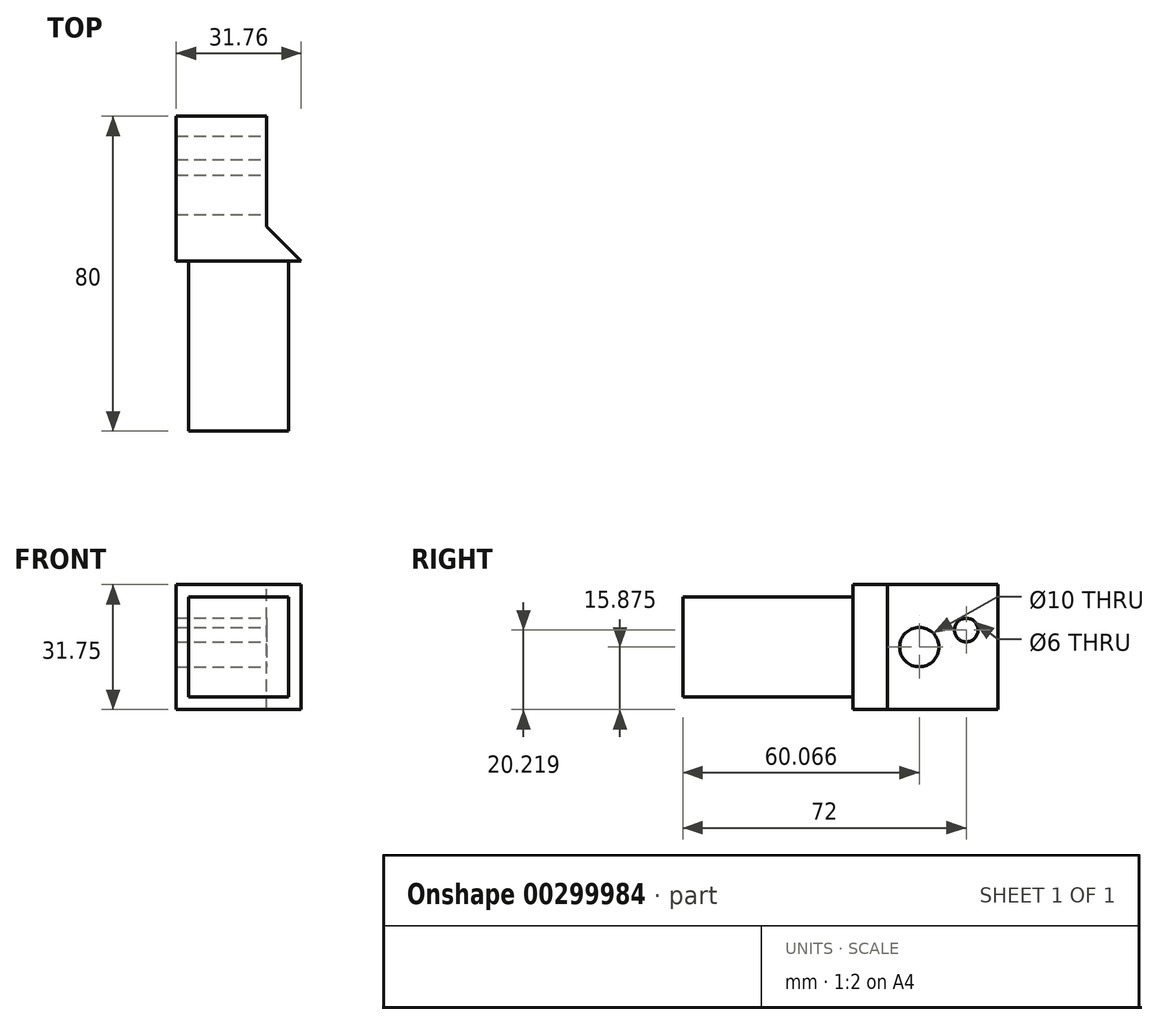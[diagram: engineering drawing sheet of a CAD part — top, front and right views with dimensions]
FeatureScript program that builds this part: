
annotation { "Feature Type Name" : "Feature", "Feature Type Description" : "" }
export const myFeature = defineFeature(function(context is Context, id is Id, definition is map)
    precondition{}
    {
        {
            var Q0;
            Q0=qCreatedBy(makeId("Top.planeOp"),FACE);
            var sketch = newSketch(context, id + "F0", { "sketchPlane" : qUnion([Q0])});
            skLineSegment(sketch, "E0.bottom", {"start": v(-15.88, 40) * mm, "end": v(15.88, 40) * mm});
            skLineSegment(sketch, "E0.top", {"start": v(-15.88, -40) * mm, "end": v(15.88, -40) * mm});
            skLineSegment(sketch, "E0.left", {"start": v(-15.88, 40) * mm, "end": v(-15.88, -40) * mm});
            skLineSegment(sketch, "E0.right", {"start": v(15.88, 40) * mm, "end": v(15.88, -40) * mm});
            skSolve(sketch);
        }
        {
            var Q0;
            Q0 = qSketchRegion(id + "F0", true);
            extrude(context, id + "F1", {"entities" : qUnion([Q0]), "depth" : 31.75 * mm, "offsetDistance" : 25 * mm});
        }
        {
            var Q0;
            Q0=makeQuery(id+"F1.opExtrude","SWEPT_FACE",FACE,{"disambiguationData":[OSD([sQuery(id+"F0.wireOp",EDGE,"E0.right")])]});
            var sketch = newSketch(context, id + "F2", { "sketchPlane" : qUnion([Q0])});
            skCircle(sketch, "E1", {"center": v(20.07, 15.88) * mm, "radius": 5 * mm});
            skCircle(sketch, "E2", {"center": v(32, 20.22) * mm, "radius": 3 * mm});
            skLineSegment(sketch, "E3", {"start": v(20.07, 15.88) * mm, "end": v(26.86, 15.88) * mm});
            skLineSegment(sketch, "E4", {"start": v(20.07, 15.88) * mm, "end": v(32, 20.22) * mm});
            skSolve(sketch);
        }
        {
            var Q0;
            Q0 = qSketchRegion(id + "F2", true);
            extrude(context, id + "F3", {"entities" : qUnion([Q0]), "operationType" : NewBodyOperationType.REMOVE, "endBound" : BoundingType.THROUGH_ALL, "oppositeDirection" : true, "depth" : 25 * mm, "offsetDistance" : 25 * mm});
        }
        {
            var Q0;
            Q0=makeQuery(id+"F1.opExtrude","CAP_FACE",FACE,{"disambiguationData":[OSD([sQuery(id+"F0.wireOp",EDGE,"E0.bottom"),sQuery(id+"F0.wireOp",EDGE,"E0.top"),sQuery(id+"F0.wireOp",EDGE,"E0.left"),sQuery(id+"F0.wireOp",EDGE,"E0.right")])],"isStart":false});
            var sketch = newSketch(context, id + "F4", { "sketchPlane" : qUnion([Q0])});
            skLineSegment(sketch, "E5", {"start": v(-12.7, -50) * mm, "end": v(-12.7, 10) * mm});
            skLineSegment(sketch, "E6", {"start": v(-12.7, 10) * mm, "end": v(12.7, 10) * mm});
            skLineSegment(sketch, "E7", {"start": v(12.7, 10) * mm, "end": v(12.7, -50) * mm});
            skLineSegment(sketch, "E8", {"start": v(12.7, -50) * mm, "end": v(-12.7, -50) * mm});
            skLineSegment(sketch, "E9", {"start": v(15.88, 40) * mm, "end": v(15.88, -63.27) * mm});
            skLineSegment(sketch, "E10", {"start": v(-12.7, 3.25) * mm, "end": v(-28.39, 3.25) * mm});
            skLineSegment(sketch, "E11", {"start": v(-28.39, 3.25) * mm, "end": v(29.3, 3.25) * mm});
            skLineSegment(sketch, "E12", {"start": v(29.3, 3.25) * mm, "end": v(29.3, -68.48) * mm});
            skLineSegment(sketch, "E13", {"start": v(29.3, -68.48) * mm, "end": v(-28.39, -68.48) * mm});
            skLineSegment(sketch, "E14", {"start": v(-28.39, -68.48) * mm, "end": v(-28.39, 3.25) * mm});
            skSolve(sketch);
        }
        {
            var Q0;
            {var subQ0=sQuery(id+"F4.wireOp",EDGE,"E8");Q0=makeQuery(id+"F4.imprint","IMPRINT",FACE,{"disambiguationData":[TD([[makeQuery(id+"F4.imprint","IMPRINT",EDGE,{"derivedFrom":subQ0}),-1.0]])]});}
            var Q1;
            {var subQ0=sQuery(id+"F4.wireOp",EDGE,"E11");var subQ1=sQuery(id+"F4.wireOp",EDGE,"E7");var subQ2=makeQuery(id+"F4.imprint","INTERSECT",VERTEX,{"derivedFrom":[subQ1,subQ0]});Q1=makeQuery(id+"F4.imprint","IMPRINT",FACE,{"disambiguationData":[TD([[makeQuery(id+"F4.imprint","IMPRINT",EDGE,{"disambiguationData":[TD([[subQ2,-1.0]])],"derivedFrom":subQ1}),1.0]])]});}
            var Q2;
            {var subQ0=sQuery(id+"F4.wireOp",EDGE,"E11");var subQ1=sQuery(id+"F4.wireOp",EDGE,"E5");var subQ2=makeQuery(id+"F4.imprint","INTERSECT",VERTEX,{"derivedFrom":[subQ1,subQ0]});Q2=makeQuery(id+"F4.imprint","IMPRINT",FACE,{"disambiguationData":[TD([[makeQuery(id+"F4.imprint","IMPRINT",EDGE,{"disambiguationData":[TD([[subQ2,1.0]])],"derivedFrom":subQ1}),1.0]])]});}
            extrude(context, id + "F5", {"entities" : qUnion([Q0, Q1, Q2]), "operationType" : NewBodyOperationType.REMOVE, "endBound" : BoundingType.THROUGH_ALL, "oppositeDirection" : true, "depth" : 25 * mm, "offsetDistance" : 25 * mm});
        }
        {
            var Q0;
            Q0=makeQuery(id+"F1.opExtrude","SWEPT_FACE",FACE,{"disambiguationData":[OSD([sQuery(id+"F0.wireOp",EDGE,"E0.right")])]});
            var sketch = newSketch(context, id + "F6", { "sketchPlane" : qUnion([Q0])});
            skLineSegment(sketch, "E15.bottom", {"start": v(3.25, 28.58) * mm, "end": v(-44.46, 28.57) * mm});
            skLineSegment(sketch, "E15.top", {"start": v(3.25, 40.72) * mm, "end": v(-44.46, 40.72) * mm});
            skLineSegment(sketch, "E15.left", {"start": v(3.25, 28.57) * mm, "end": v(3.25, 40.72) * mm});
            skLineSegment(sketch, "E15.right", {"start": v(-44.46, 28.57) * mm, "end": v(-44.46, 40.72) * mm});
            skLineSegment(sketch, "E16.bottom", {"start": v(3.25, 3.17) * mm, "end": v(-44.46, 3.17) * mm});
            skLineSegment(sketch, "E16.top", {"start": v(3.25, -7.24) * mm, "end": v(-44.46, -7.24) * mm});
            skLineSegment(sketch, "E16.left", {"start": v(3.25, 3.17) * mm, "end": v(3.25, -7.24) * mm});
            skLineSegment(sketch, "E16.right", {"start": v(-44.46, 3.17) * mm, "end": v(-44.46, -7.24) * mm});
            skSolve(sketch);
        }
        {
            var Q0;
            Q0 = qSketchRegion(id + "F6", true);
            extrude(context, id + "F7", {"entities" : qUnion([Q0]), "operationType" : NewBodyOperationType.REMOVE, "endBound" : BoundingType.THROUGH_ALL, "oppositeDirection" : true, "depth" : 25 * mm, "offsetDistance" : 25 * mm});
        }
        {
            var Q0;
            Q0=makeQuery(id+"F1.opExtrude","CAP_FACE",FACE,{"disambiguationData":[OSD([sQuery(id+"F0.wireOp",EDGE,"E0.bottom"),sQuery(id+"F0.wireOp",EDGE,"E0.top"),sQuery(id+"F0.wireOp",EDGE,"E0.left"),sQuery(id+"F0.wireOp",EDGE,"E0.right")])],"isStart":false});
            var sketch = newSketch(context, id + "F8", { "sketchPlane" : qUnion([Q0])});
            skLineSegment(sketch, "E17.bottom", {"start": v(15.88, 40) * mm, "end": v(7.12, 40) * mm});
            skLineSegment(sketch, "E17.top", {"start": v(15.88, 3.25) * mm, "end": v(7.12, 3.25) * mm});
            skLineSegment(sketch, "E17.left", {"start": v(15.88, 40) * mm, "end": v(15.88, 3.25) * mm});
            skLineSegment(sketch, "E17.right", {"start": v(7.12, 40) * mm, "end": v(7.13, 3.25) * mm});
            skLineSegment(sketch, "E18", {"start": v(15.88, 3.25) * mm, "end": v(7.12, 12) * mm});
            skSolve(sketch);
        }
        {
            var Q0;
            {var subQ0=sQuery(id+"F8.wireOp",EDGE,"E17.bottom");Q0=makeQuery(id+"F8.imprint","IMPRINT",FACE,{"disambiguationData":[TD([[makeQuery(id+"F8.imprint","IMPRINT",EDGE,{"derivedFrom":subQ0}),-1.0]])]});}
            extrude(context, id + "F9", {"entities" : qUnion([Q0]), "operationType" : NewBodyOperationType.REMOVE, "endBound" : BoundingType.THROUGH_ALL, "oppositeDirection" : true, "depth" : 25.4 * mm, "offsetDistance" : 25.4 * mm});
        }
    });
